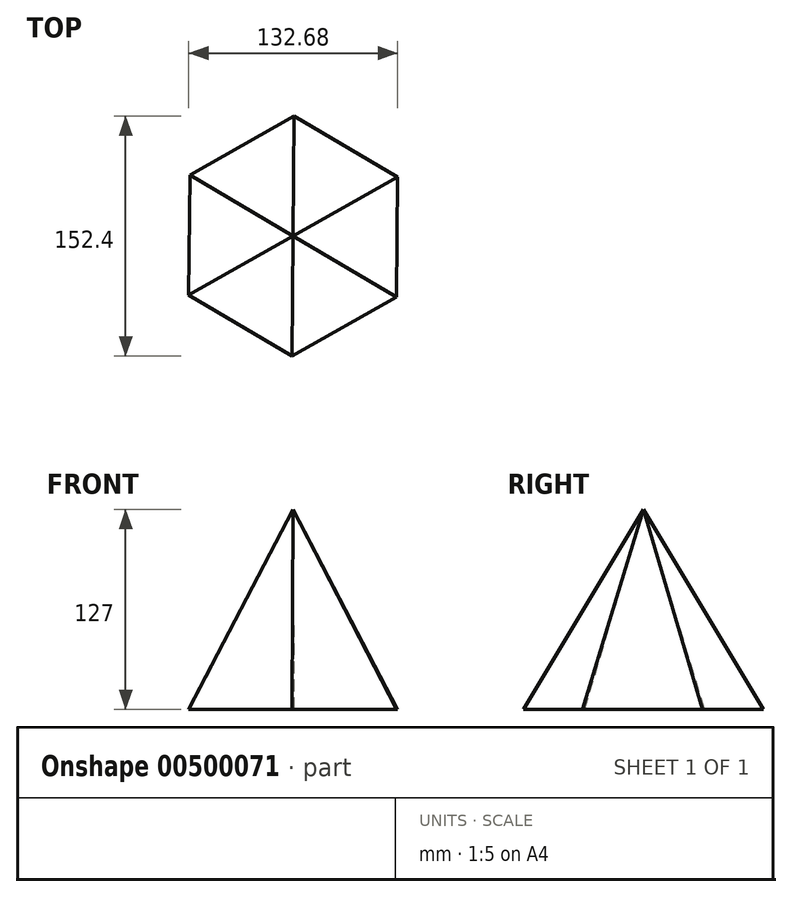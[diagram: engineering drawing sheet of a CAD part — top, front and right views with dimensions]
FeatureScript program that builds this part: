
annotation { "Feature Type Name" : "Feature", "Feature Type Description" : "" }
export const myFeature = defineFeature(function(context is Context, id is Id, definition is map)
    precondition{}
    {
        {
            var Q0;
            Q0=qCreatedBy(makeId("Top.planeOp"),FACE);
            var sketch = newSketch(context, id + "F0", { "sketchPlane" : qUnion([Q0])});
            skCircle(sketch, "E0.cCircle", {"center": v(0, 0) * mm, "radius": 76.2 * mm, "construction": true});
            skLineSegment(sketch, "E0.0", {"start": v(65.64, -38.7) * mm, "end": v(-0.7, -76.2) * mm});
            skLineSegment(sketch, "E0.1", {"start": v(-0.7, -76.2) * mm, "end": v(-66.34, -37.49) * mm});
            skLineSegment(sketch, "E0.2", {"start": v(-66.34, -37.49) * mm, "end": v(-65.64, 38.7) * mm});
            skLineSegment(sketch, "E0.3", {"start": v(-65.64, 38.7) * mm, "end": v(0.7, 76.2) * mm});
            skLineSegment(sketch, "E0.4", {"start": v(0.7, 76.2) * mm, "end": v(66.34, 37.49) * mm});
            skLineSegment(sketch, "E0.5", {"start": v(66.34, 37.49) * mm, "end": v(65.64, -38.7) * mm});
            skSolve(sketch);
        }
        {
            var Q0;
            Q0=qCreatedBy(makeId("Top.planeOp"),FACE);
            cPlane(context, id + "F1", {"entities" : qUnion([Q0]), "cplaneType" : CPlaneType.OFFSET, "offset" : 127 * mm, "width" : 152.4 * mm, "height" : 152.4 * mm});
        }
        {
            var Q0;
            Q0=qCreatedBy(id+"F1.planeOp",FACE);
            var sketch = newSketch(context, id + "F2", { "sketchPlane" : qUnion([Q0])});
            skPoint(sketch, "E1", {"position": v(0, 0) * mm});
            skSolve(sketch);
        }
        {
            var Q0;
            Q0=makeQuery(id+"F0.imprint","IMPRINT",FACE,{"disambiguationData":[TD([[makeQuery(id+"F0.imprint","IMPRINT",EDGE,{"derivedFrom":sQuery(id+"F0.wireOp",EDGE,"E0.0")}),-1.0]])]});
            var Q1;
            Q1=sQuery(id+"F2.wireOp",VERTEX,"E1");
            loft(context, id + "F3", {"sheetProfilesArray" : [{ "sheetProfileEntities" : qUnion([Q0]) }, { "sheetProfileEntities" : qUnion([Q1]) }]});
        }
    });
